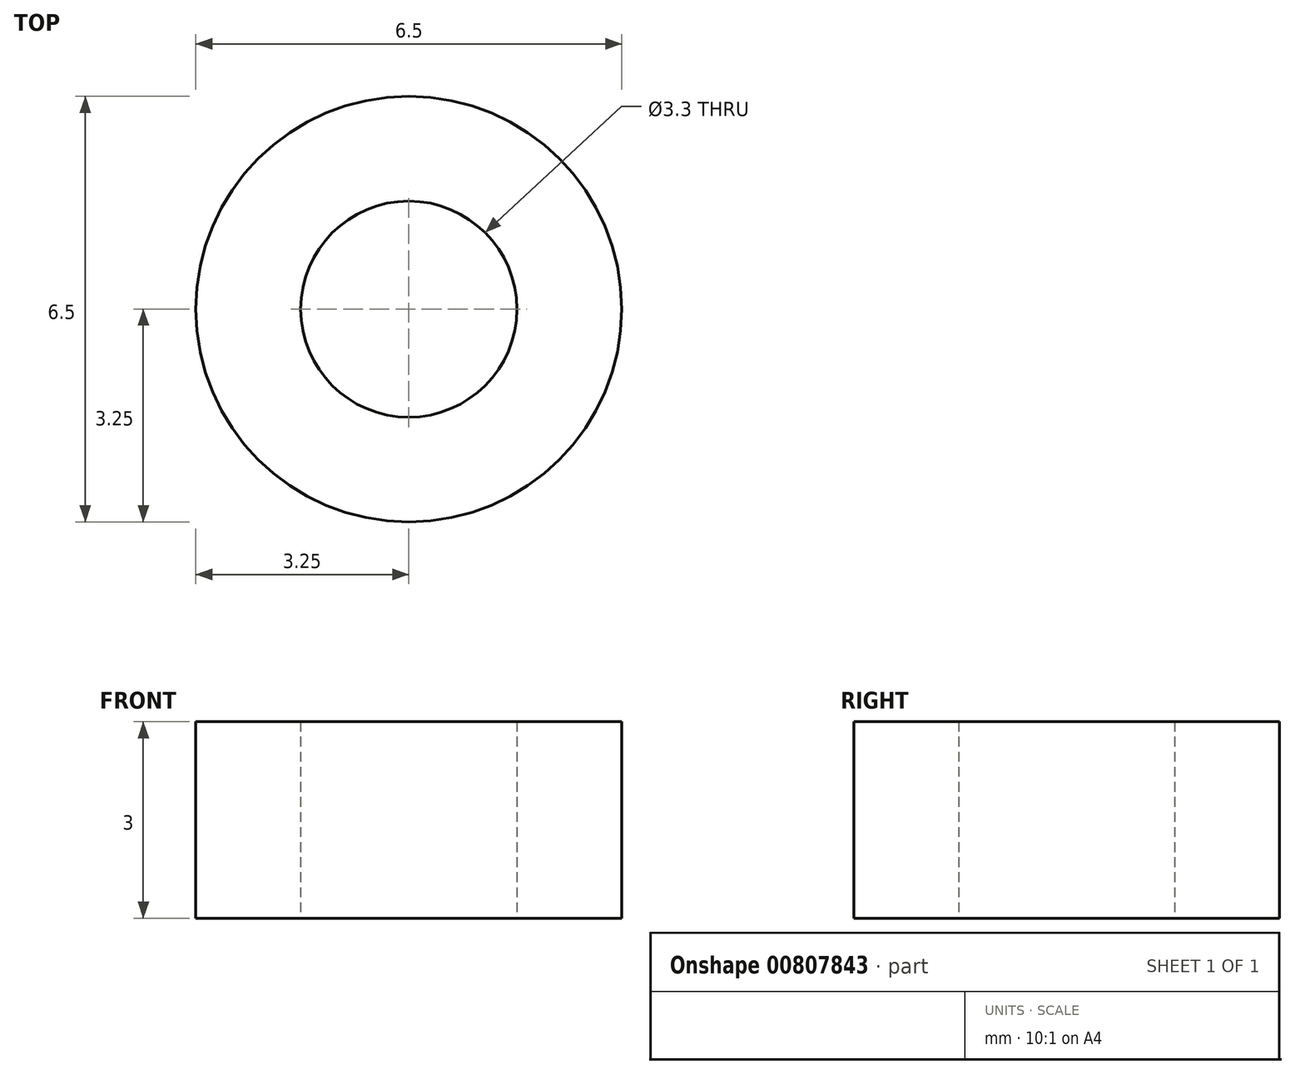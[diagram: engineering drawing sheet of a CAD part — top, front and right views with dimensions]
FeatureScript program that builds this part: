
annotation { "Feature Type Name" : "Feature", "Feature Type Description" : "" }
export const myFeature = defineFeature(function(context is Context, id is Id, definition is map)
    precondition{}
    {
        {
            var Q0;
            Q0=qCreatedBy(makeId("Top.planeOp"),FACE);
            var sketch = newSketch(context, id + "F0", { "sketchPlane" : qUnion([Q0])});
            skCircle(sketch, "E0", {"center": v(0, 0) * mm, "radius": 1.65 * mm});
            skCircle(sketch, "E1", {"center": v(0, 0) * mm, "radius": 3.25 * mm});
            skSolve(sketch);
        }
        {
            var Q0;
            Q0=makeQuery(id+"F0.imprint","IMPRINT",FACE,{"disambiguationData":[TD([[makeQuery(id+"F0.imprint","IMPRINT",EDGE,{"derivedFrom":sQuery(id+"F0.wireOp",EDGE,"E0")}),-1.0]])]});
            extrude(context, id + "F1", {"entities" : qUnion([Q0]), "depth" : 3 * mm, "offsetDistance" : 25 * mm});
        }
    });
